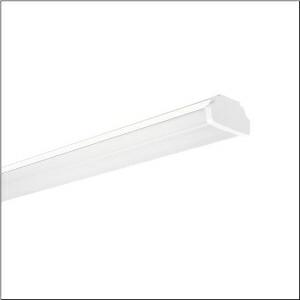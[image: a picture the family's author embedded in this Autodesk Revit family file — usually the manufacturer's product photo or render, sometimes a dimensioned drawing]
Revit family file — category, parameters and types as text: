
# Revit family: modario_31_gen_2_53bm812cv49xc2_7681
name_source: partatom
category: Lighting Fixtures
units: mm (PartAtom-declared; Revit-internal decimal feet)

## family parameters
Cut with Voids When Loaded = No
Host = Face
Light Source = No
Part Type = Normal
Room Calculation Point = No
Round Connector Dimension = Use Diameter
Shared = No

## types (1)
- --- (1 x LED, 9240 lm, 49.9 W, 4000K)
    Apparent Load = 50 VA
    CIE Flux Codes = 47 80 95 93 100
    Color Rendering = 80
    Color Temperature = 4000K
    Default Elevation = 1800 mm
    Description = Modario 31 Gen.2, luminaire insert, of sheet steel, coil coated, white, length: 1.495mm, width: 81mm, height: 82mm, 5x system unit, system units: 299mm, LED rated luminous flux: 9.240lm, light colour: 840, SDCM (Standard Deviation of Colour Matching)MacAdam ≤ 3 SDCM (initial), control gear: ON/OFF Multilumen, CLOi, with plug, 3-pole, with phase selection, mains connection: 220..240V, AC, 50/60Hz, start of lifetime: 50W, end of service life: 61W, through-wiring accessed according to module size, primary optical cover: cover, of PMMA, light emission: direct distribution, primary light characteristic: symmetric, protection rating (complete): IP20, protection rating (LED compartment): IP50, insulation class (complete): insulation class I (protective earthing), certification: CE, ENEC, VDE, UKCA, impact resistance: IK03, permissible ambient temperature for indoor applications: -35..+40°C, corresponds to IFS (International Featured Standards) requirements for safety and quality in the food industry, reducing of maximum allowable ambient temperature of 5°C with ceiling mounting, IP40 when using the optional accessory 5TP9018, packaging unit: 1 piece
    Height = 92 mm
    Lamp = 1 x LED
    Lamp Light Flux = 9240 lm
    Lamp Power = 49.9 W
    Lamp count = 1
    Length = 1495 mm
    Luminous efficacy = 185 lm/W
    Manufacturer = Siteco
    ModVariant = No
    Model = 53BM812CV49XC2
    Mounting Place = Ceiling
    Mounting Type = Pendant
    Number of Poles = 1
    OnlyDefault = Yes
    Power Factor = 1
    Product Name = Modario 31 Gen.2
    Product group = luminaire insert | ceiling pendant
    ProductGroupID = 901
    Protection Class = Protection class I
    Protection Degree = IP 20
    RLX_Detail_Level = 1
    RLX_Emergency_Light_Flux = 0 lm
    RLX_Emergency_Type = 0
    RLX_Emergency_Type_DB = No
    RlxData = <blob elided: 40133 chars, md5=07640a3d>
    Socket = socket
    Standby Power = 0 W
    System Light Flux = 9240 lm
    System Power = 50 W
    Type Comments = factory setting: luminous flux: 100 % | (A | C | E) | 116 mA
    Type Image = l_1341886.jpg
    URL = http://relux.com
    VarID = @adj_050785
    Voltage = 0 V
    Weight = 0.00 kg
    Width = 81 mm

## geometry (parser evidence)
native form markers: Blend x4, Sweep x13
no freeform markers — native parametric forms only
